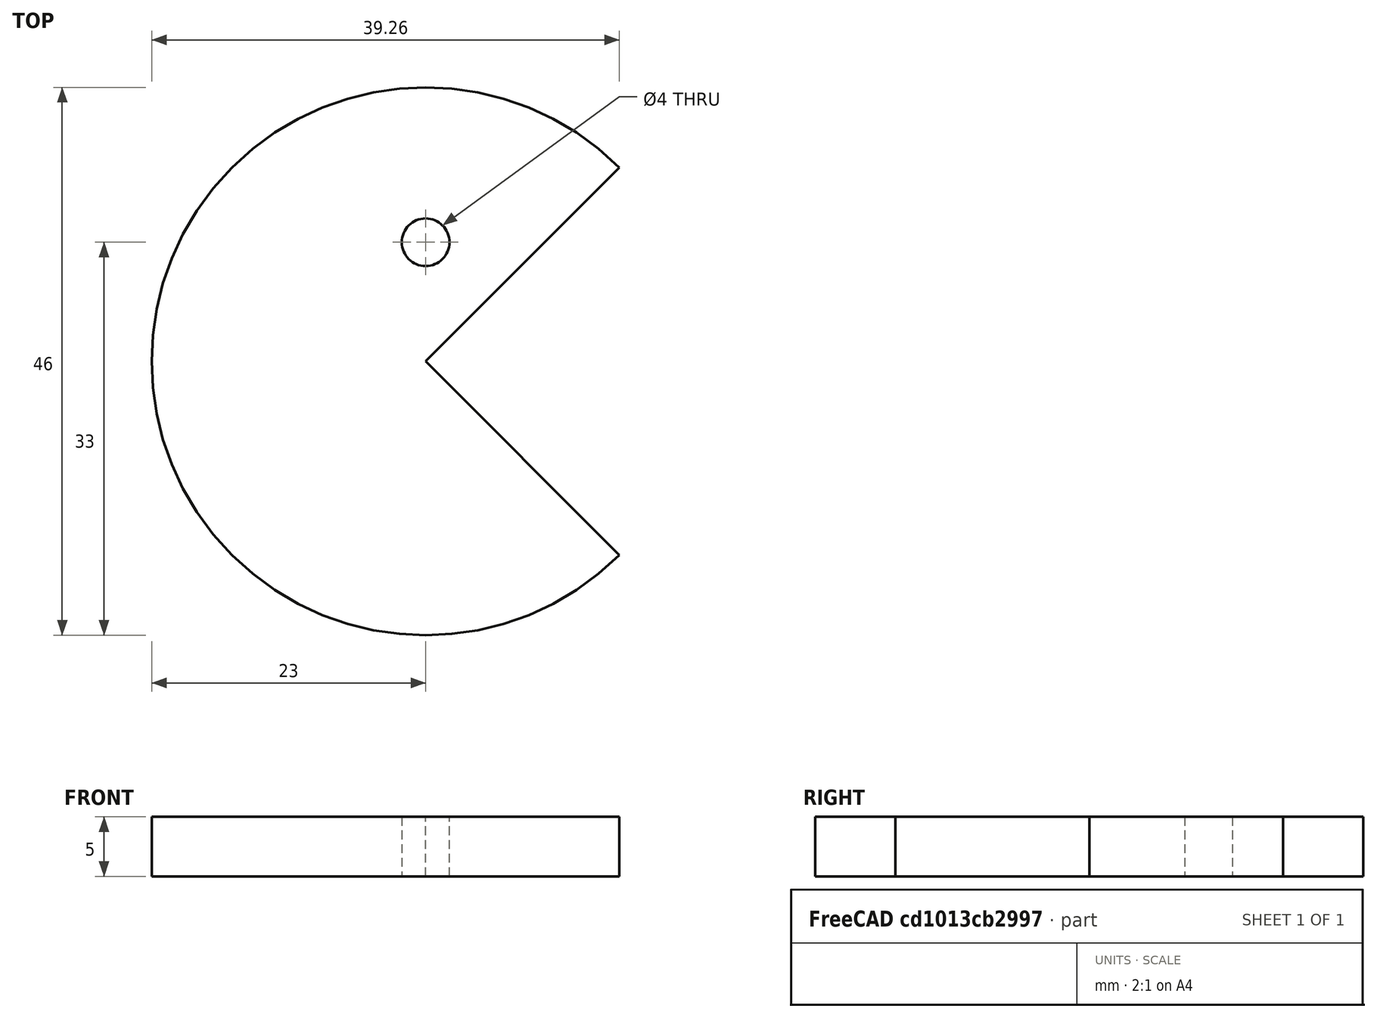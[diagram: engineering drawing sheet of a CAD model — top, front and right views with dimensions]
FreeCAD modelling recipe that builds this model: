
FCSTD DOCUMENT  (FreeCAD 0.21R33694 (Git))
Label: OJT1_T09_R01_Pacman
License: All rights reserved
LicenseURL: https://en.wikipedia.org/wiki/All_rights_reserved
objects: Part::Cylinder×2, Part::Cut×1
note: 3 computed .brp shape members not serialized (recipe doc carries the construction recipe); baked Part::Feature solids carry a one-line shape summary decoded from their .brp

FEATURE [Part::Cylinder] Cylinder  label="Pacman"
  Angle = 270
  AttacherType = Attacher::AttachEngine3D
  FirstAngle = 0
  Height = 5
  Placement = pos=(0,0,0) rot=(0,0,1;0.785398rad)
  Radius = 23
  SecondAngle = 0
  expr: .Placement.Base.z = 0 mm
  expr: .Placement.Rotation.Yaw = 45
FEATURE [Part::Cylinder] Cylinder001  label="Ojo"
  Angle = 360
  AttacherType = Attacher::AttachEngine3D
  FirstAngle = 0
  Height = 10
  Placement = pos=(0,10,-3) rot=(0,0,1;0rad)
  Radius = 2
  SecondAngle = 0
  expr: .Placement.Base.y = 10 mm
FEATURE [Part::Cut] Cut  label="Pacman001"
  Base = -> Cylinder
  Tool = -> Cylinder001
